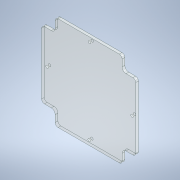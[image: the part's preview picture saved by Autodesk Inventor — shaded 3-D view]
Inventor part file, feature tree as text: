
AUTODESK INVENTOR PART (.ipt)
format: ipt  version: 2021 (Build 250183000, 183)  size: 334,336 bytes
history: native  units: mm
features: other x2, plane x1, extrude x1, sketch x1, reference x1, projected_geometry x1
ambient origin geometry x8: Origin, YZ Plane, XZ Plane, XY Plane, X Axis, Y Axis, Z Axis, Center Point
bodies: Body1 (feature_tree)
feature tree (7):
  plane  "Work Plane1"
  extrude  "Extrusion3"  Depth=8.0mm
  sketch  "Sketch6"  dims[d19=8.0mm d20=0.0mm d21=1.5mm d22=2.5mm d23=2.5mm d24=2.5mm d25=1.5mm d26=7.5mm d27=7.5mm d28=7.5mm d29=7.5mm d30=7.5mm]
  reference  "Reference1"
  projected_geometry  "Projected Loop3"
  other  "Assembly1"
  other  "MDF_Block:1"
